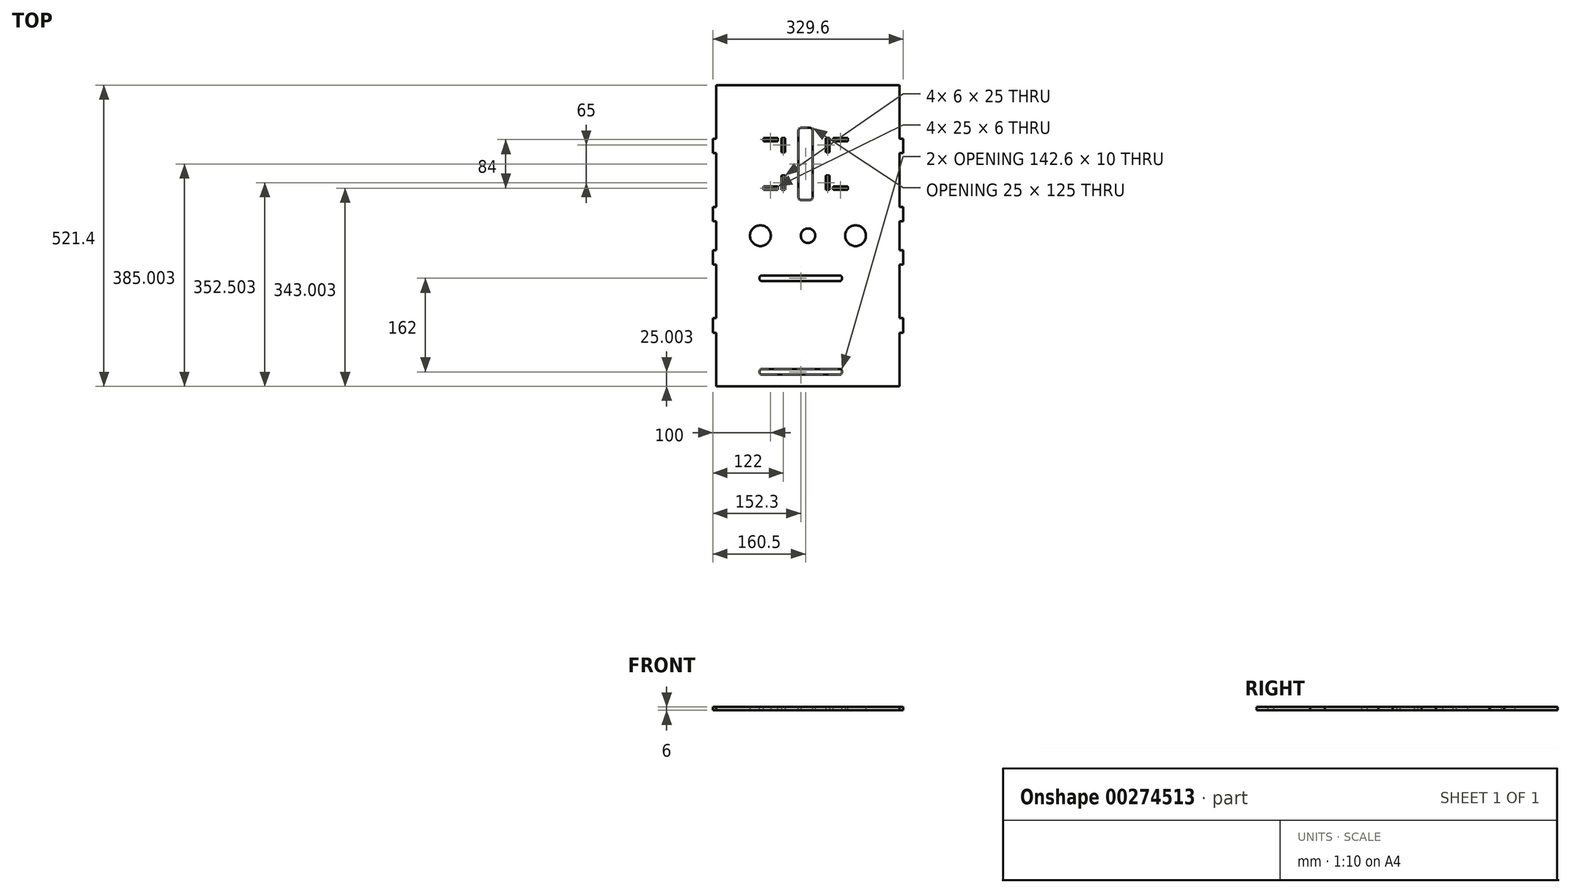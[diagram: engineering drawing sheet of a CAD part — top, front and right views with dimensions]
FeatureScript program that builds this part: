
annotation { "Feature Type Name" : "Feature", "Feature Type Description" : "" }
export const myFeature = defineFeature(function(context is Context, id is Id, definition is map)
    precondition{}
    {
        {
            var Q0;
            Q0=qCreatedBy(makeId("Top.planeOp"),FACE);
            var sketch = newSketch(context, id + "F0", { "sketchPlane" : qUnion([Q0])});
            skLineSegment(sketch, "E0.bottom", {"start": v(-164.8, 495.45) * mm, "end": v(164.8, 495.45) * mm});
            skLineSegment(sketch, "E0.top", {"start": v(-164.8, -25.95) * mm, "end": v(164.8, -25.95) * mm});
            skLineSegment(sketch, "E0.left", {"start": v(-164.8, 495.45) * mm, "end": v(-164.8, -25.95) * mm});
            skLineSegment(sketch, "E0.right", {"start": v(164.8, 495.45) * mm, "end": v(164.8, -25.95) * mm});
            skCircle(sketch, "E1", {"center": v(0, 234.75) * mm, "radius": 12.5 * mm});
            skCircle(sketch, "E2", {"center": v(-82.4, 234.75) * mm, "radius": 18 * mm});
            skCircle(sketch, "E3", {"center": v(82.4, 234.75) * mm, "radius": 18 * mm});
            skLineSegment(sketch, "E4.bottom", {"start": v(-45.8, 404.05) * mm, "end": v(-39.8, 404.05) * mm});
            skLineSegment(sketch, "E4.top", {"start": v(-45.8, 379.05) * mm, "end": v(-39.8, 379.05) * mm});
            skLineSegment(sketch, "E4.left", {"start": v(-45.8, 404.05) * mm, "end": v(-45.8, 379.05) * mm});
            skLineSegment(sketch, "E4.right", {"start": v(-39.8, 404.05) * mm, "end": v(-39.8, 379.05) * mm});
            skLineSegment(sketch, "E5.bottom", {"start": v(-45.8, 339.05) * mm, "end": v(-39.8, 339.05) * mm});
            skLineSegment(sketch, "E5.top", {"start": v(-45.8, 314.05) * mm, "end": v(-39.8, 314.05) * mm});
            skLineSegment(sketch, "E5.left", {"start": v(-45.8, 339.05) * mm, "end": v(-45.8, 314.05) * mm});
            skLineSegment(sketch, "E5.right", {"start": v(-39.8, 339.05) * mm, "end": v(-39.8, 314.05) * mm});
            skLineSegment(sketch, "E6.bottom", {"start": v(31.2, 404.05) * mm, "end": v(37.2, 404.05) * mm});
            skLineSegment(sketch, "E6.top", {"start": v(31.2, 379.05) * mm, "end": v(37.2, 379.05) * mm});
            skLineSegment(sketch, "E6.left", {"start": v(31.2, 404.05) * mm, "end": v(31.2, 379.05) * mm});
            skLineSegment(sketch, "E6.right", {"start": v(37.2, 404.05) * mm, "end": v(37.2, 379.05) * mm});
            skLineSegment(sketch, "E7.bottom", {"start": v(31.2, 339.05) * mm, "end": v(37.2, 339.05) * mm});
            skLineSegment(sketch, "E7.top", {"start": v(31.2, 314.05) * mm, "end": v(37.2, 314.05) * mm});
            skLineSegment(sketch, "E7.left", {"start": v(31.2, 339.05) * mm, "end": v(31.2, 314.05) * mm});
            skLineSegment(sketch, "E7.right", {"start": v(37.2, 339.05) * mm, "end": v(37.2, 314.05) * mm});
            skSolve(sketch);
        }
        {
            var Q0;
            Q0 = qSketchRegion(id + "F0", true);
            extrude(context, id + "F1", {"entities" : qUnion([Q0]), "depth" : 6 * mm});
        }
        {
            var Q0;
            Q0=makeQuery(id+"F1.opExtrude","CAP_FACE",FACE,{"disambiguationData":[OSD([sQuery(id+"F0.wireOp",EDGE,"E0.bottom"),sQuery(id+"F0.wireOp",EDGE,"E0.top"),sQuery(id+"F0.wireOp",EDGE,"E0.left"),sQuery(id+"F0.wireOp",EDGE,"E0.right"),sQuery(id+"F0.wireOp",EDGE,"E1")])],"isStart":false});
            var sketch = newSketch(context, id + "F2", { "sketchPlane" : qUnion([Q0])});
            skLineSegment(sketch, "E8.bottom", {"start": v(-164.8, 495.45) * mm, "end": v(-158.8, 495.45) * mm});
            skLineSegment(sketch, "E8.top", {"start": v(-164.8, 402.6) * mm, "end": v(-158.8, 402.6) * mm});
            skLineSegment(sketch, "E8.left", {"start": v(-164.8, 495.45) * mm, "end": v(-164.8, 402.6) * mm});
            skLineSegment(sketch, "E8.right", {"start": v(-158.8, 495.45) * mm, "end": v(-158.8, 402.6) * mm});
            skLineSegment(sketch, "E9.bottom", {"start": v(-164.8, 377.6) * mm, "end": v(-158.8, 377.6) * mm});
            skLineSegment(sketch, "E9.top", {"start": v(-164.8, 284.75) * mm, "end": v(-158.8, 284.75) * mm});
            skLineSegment(sketch, "E9.left", {"start": v(-164.8, 377.6) * mm, "end": v(-164.8, 284.75) * mm});
            skLineSegment(sketch, "E9.right", {"start": v(-158.8, 377.6) * mm, "end": v(-158.8, 284.75) * mm});
            skLineSegment(sketch, "E10.bottom", {"start": v(-164.8, 259.75) * mm, "end": v(-158.8, 259.75) * mm});
            skLineSegment(sketch, "E10.top", {"start": v(-164.8, 209.75) * mm, "end": v(-158.8, 209.75) * mm});
            skLineSegment(sketch, "E10.left", {"start": v(-164.8, 259.75) * mm, "end": v(-164.8, 209.75) * mm});
            skLineSegment(sketch, "E10.right", {"start": v(-158.8, 259.75) * mm, "end": v(-158.8, 209.75) * mm});
            skLineSegment(sketch, "E11.bottom", {"start": v(-164.8, 184.75) * mm, "end": v(-158.8, 184.75) * mm});
            skLineSegment(sketch, "E11.top", {"start": v(-164.8, 91.9) * mm, "end": v(-158.8, 91.9) * mm});
            skLineSegment(sketch, "E11.left", {"start": v(-164.8, 184.75) * mm, "end": v(-164.8, 91.9) * mm});
            skLineSegment(sketch, "E11.right", {"start": v(-158.8, 184.75) * mm, "end": v(-158.8, 91.9) * mm});
            skLineSegment(sketch, "E12.bottom", {"start": v(-164.8, -25.95) * mm, "end": v(-158.8, -25.95) * mm});
            skLineSegment(sketch, "E12.top", {"start": v(-164.8, 66.9) * mm, "end": v(-158.8, 66.9) * mm});
            skLineSegment(sketch, "E12.left", {"start": v(-164.8, -25.95) * mm, "end": v(-164.8, 66.9) * mm});
            skLineSegment(sketch, "E12.right", {"start": v(-158.8, -25.95) * mm, "end": v(-158.8, 66.9) * mm});
            skLineSegment(sketch, "E13", {"start": v(0, 495.45) * mm, "end": v(0, -25.95) * mm});
            skLineSegment(sketch, "E14.MirrorCS", {"start": v(164.8, 402.6) * mm, "end": v(158.8, 402.6) * mm});
            skLineSegment(sketch, "E15.MirrorCS", {"start": v(164.8, 66.9) * mm, "end": v(158.8, 66.9) * mm});
            skLineSegment(sketch, "E16.MirrorCS", {"start": v(164.8, 184.75) * mm, "end": v(158.8, 184.75) * mm});
            skLineSegment(sketch, "E17.MirrorCS", {"start": v(164.8, 377.6) * mm, "end": v(158.8, 377.6) * mm});
            skLineSegment(sketch, "E18.MirrorCS", {"start": v(164.8, 495.45) * mm, "end": v(158.8, 495.45) * mm});
            skLineSegment(sketch, "E19.MirrorCS", {"start": v(164.8, 284.75) * mm, "end": v(158.8, 284.75) * mm});
            skLineSegment(sketch, "E20.MirrorCS", {"start": v(164.8, -25.95) * mm, "end": v(158.8, -25.95) * mm});
            skLineSegment(sketch, "E21.MirrorCS", {"start": v(164.8, 209.75) * mm, "end": v(158.8, 209.75) * mm});
            skLineSegment(sketch, "E22.MirrorCS", {"start": v(164.8, 91.9) * mm, "end": v(158.8, 91.9) * mm});
            skLineSegment(sketch, "E23.MirrorCS", {"start": v(164.8, 259.75) * mm, "end": v(158.8, 259.75) * mm});
            skLineSegment(sketch, "E24.MirrorCS", {"start": v(158.8, -25.95) * mm, "end": v(158.8, 66.9) * mm});
            skLineSegment(sketch, "E25.MirrorCS", {"start": v(164.8, 495.45) * mm, "end": v(164.8, 402.6) * mm});
            skLineSegment(sketch, "E26.MirrorCS", {"start": v(158.8, 184.75) * mm, "end": v(158.8, 91.9) * mm});
            skLineSegment(sketch, "E27.MirrorCS", {"start": v(164.8, 377.6) * mm, "end": v(164.8, 284.75) * mm});
            skLineSegment(sketch, "E28.MirrorCS", {"start": v(158.8, 377.6) * mm, "end": v(158.8, 284.75) * mm});
            skLineSegment(sketch, "E29.MirrorCS", {"start": v(164.8, -25.95) * mm, "end": v(164.8, 66.9) * mm});
            skLineSegment(sketch, "E30.MirrorCS", {"start": v(158.8, 495.45) * mm, "end": v(158.8, 402.6) * mm});
            skLineSegment(sketch, "E31.MirrorCS", {"start": v(164.8, 259.75) * mm, "end": v(164.8, 209.75) * mm});
            skLineSegment(sketch, "E32.MirrorCS", {"start": v(158.8, 259.75) * mm, "end": v(158.8, 209.75) * mm});
            skLineSegment(sketch, "E33.MirrorCS", {"start": v(164.8, 184.75) * mm, "end": v(164.8, 91.9) * mm});
            skSolve(sketch);
        }
        {
            var Q0;
            Q0 = qSketchRegion(id + "F2", true);
            extrude(context, id + "F3", {"entities" : qUnion([Q0]), "operationType" : NewBodyOperationType.REMOVE, "oppositeDirection" : true, "depth" : 25 * mm});
        }
        {
            var Q0;
            Q0=makeQuery(id+"F1.opExtrude","CAP_FACE",FACE,{"disambiguationData":[OSD([sQuery(id+"F0.wireOp",EDGE,"E0.bottom"),sQuery(id+"F0.wireOp",EDGE,"E0.top"),sQuery(id+"F0.wireOp",EDGE,"E0.left"),sQuery(id+"F0.wireOp",EDGE,"E0.right"),sQuery(id+"F0.wireOp",EDGE,"E1")])],"isStart":false});
            var sketch = newSketch(context, id + "F4", { "sketchPlane" : qUnion([Q0])});
            skLineSegment(sketch, "E34.bottom", {"start": v(-79.8, 166.05) * mm, "end": v(54.8, 166.05) * mm});
            skLineSegment(sketch, "E34.top", {"start": v(-79.8, 156.05) * mm, "end": v(54.8, 156.05) * mm});
            skLineSegment(sketch, "E34.left", {"start": v(-83.8, 162.05) * mm, "end": v(-83.8, 160.05) * mm});
            skLineSegment(sketch, "E34.right", {"start": v(58.8, 162.05) * mm, "end": v(58.8, 160.05) * mm});
            skLineSegment(sketch, "E35.bottom", {"start": v(-79.8, 4.05) * mm, "end": v(54.8, 4.05) * mm});
            skLineSegment(sketch, "E35.top", {"start": v(-79.8, -5.95) * mm, "end": v(54.8, -5.95) * mm});
            skLineSegment(sketch, "E35.left", {"start": v(-83.8, 0.05) * mm, "end": v(-83.8, -1.95) * mm});
            skLineSegment(sketch, "E35.right", {"start": v(58.8, 0.05) * mm, "end": v(58.8, -1.95) * mm});
            skPoint(sketch, "E36.visualSharp", {"position": v(-83.8, 166.05) * mm});
            skArc(sketch, "E36.filletArc", {"start": v(-79.8, 166.05) * mm, "mid": v(-82.63, 164.88) * mm, "end": v(-83.8, 162.05) * mm});
            skPoint(sketch, "E37.visualSharp", {"position": v(58.8, 156.05) * mm});
            skArc(sketch, "E37.filletArc", {"start": v(54.8, 156.05) * mm, "mid": v(57.63, 157.22) * mm, "end": v(58.8, 160.05) * mm});
            skPoint(sketch, "E38.visualSharp", {"position": v(58.8, 166.05) * mm});
            skArc(sketch, "E38.filletArc", {"start": v(58.8, 162.05) * mm, "mid": v(57.63, 164.88) * mm, "end": v(54.8, 166.05) * mm});
            skPoint(sketch, "E39.visualSharp", {"position": v(-83.8, 4.05) * mm});
            skArc(sketch, "E39.filletArc", {"start": v(-79.8, 4.05) * mm, "mid": v(-82.63, 2.88) * mm, "end": v(-83.8, 0.05) * mm});
            skPoint(sketch, "E40.visualSharp", {"position": v(58.8, 4.05) * mm});
            skArc(sketch, "E40.filletArc", {"start": v(58.8, 0.05) * mm, "mid": v(57.63, 2.88) * mm, "end": v(54.8, 4.05) * mm});
            skPoint(sketch, "E41.visualSharp", {"position": v(58.8, -5.95) * mm});
            skArc(sketch, "E41.filletArc", {"start": v(54.8, -5.95) * mm, "mid": v(57.63, -4.78) * mm, "end": v(58.8, -1.95) * mm});
            skPoint(sketch, "E42.visualSharp", {"position": v(-83.8, -5.95) * mm});
            skArc(sketch, "E42.filletArc", {"start": v(-83.8, -1.95) * mm, "mid": v(-82.63, -4.78) * mm, "end": v(-79.8, -5.95) * mm});
            skPoint(sketch, "E43.visualSharp", {"position": v(-83.8, 156.05) * mm});
            skArc(sketch, "E43.filletArc", {"start": v(-83.8, 160.05) * mm, "mid": v(-82.63, 157.22) * mm, "end": v(-79.8, 156.05) * mm});
            skSolve(sketch);
        }
        {
            var Q0;
            Q0=makeQuery(id+"F1.opExtrude","CAP_FACE",FACE,{"disambiguationData":[OSD([sQuery(id+"F0.wireOp",EDGE,"E0.bottom"),sQuery(id+"F0.wireOp",EDGE,"E0.top"),sQuery(id+"F0.wireOp",EDGE,"E0.left"),sQuery(id+"F0.wireOp",EDGE,"E0.right"),sQuery(id+"F0.wireOp",EDGE,"E1"),sQuery(id+"F0.wireOp",EDGE,"E2"),sQuery(id+"F0.wireOp",EDGE,"E3"),sQuery(id+"F0.wireOp",EDGE,"E4.bottom"),sQuery(id+"F0.wireOp",EDGE,"E4.top"),sQuery(id+"F0.wireOp",EDGE,"E4.left"),sQuery(id+"F0.wireOp",EDGE,"E4.right"),sQuery(id+"F0.wireOp",EDGE,"E5.bottom"),sQuery(id+"F0.wireOp",EDGE,"E5.top"),sQuery(id+"F0.wireOp",EDGE,"E5.left"),sQuery(id+"F0.wireOp",EDGE,"E5.right"),sQuery(id+"F0.wireOp",EDGE,"E6.bottom"),sQuery(id+"F0.wireOp",EDGE,"E6.top"),sQuery(id+"F0.wireOp",EDGE,"E6.left"),sQuery(id+"F0.wireOp",EDGE,"E6.right"),sQuery(id+"F0.wireOp",EDGE,"E7.bottom"),sQuery(id+"F0.wireOp",EDGE,"E7.top"),sQuery(id+"F0.wireOp",EDGE,"E7.left"),sQuery(id+"F0.wireOp",EDGE,"E7.right")])],"isStart":false});
            var sketch = newSketch(context, id + "F5", { "sketchPlane" : qUnion([Q0])});
            skLineSegment(sketch, "E44.bottom", {"start": v(-77.3, 320.05) * mm, "end": v(-52.3, 320.05) * mm});
            skLineSegment(sketch, "E44.top", {"start": v(-77.3, 314.05) * mm, "end": v(-52.3, 314.05) * mm});
            skLineSegment(sketch, "E44.left", {"start": v(-77.3, 320.05) * mm, "end": v(-77.3, 314.05) * mm});
            skLineSegment(sketch, "E44.right", {"start": v(-52.3, 320.05) * mm, "end": v(-52.3, 314.05) * mm});
            skLineSegment(sketch, "E45.bottom", {"start": v(-52.3, 404.05) * mm, "end": v(-77.3, 404.05) * mm});
            skLineSegment(sketch, "E45.top", {"start": v(-52.3, 398.05) * mm, "end": v(-77.3, 398.05) * mm});
            skLineSegment(sketch, "E45.left", {"start": v(-52.3, 404.05) * mm, "end": v(-52.3, 398.05) * mm});
            skLineSegment(sketch, "E45.right", {"start": v(-77.3, 404.05) * mm, "end": v(-77.3, 398.05) * mm});
            skLineSegment(sketch, "E46.bottom", {"start": v(43.7, 404.05) * mm, "end": v(68.7, 404.05) * mm});
            skLineSegment(sketch, "E46.top", {"start": v(43.7, 398.05) * mm, "end": v(68.7, 398.05) * mm});
            skLineSegment(sketch, "E46.left", {"start": v(43.7, 404.05) * mm, "end": v(43.7, 398.05) * mm});
            skLineSegment(sketch, "E46.right", {"start": v(68.7, 404.05) * mm, "end": v(68.7, 398.05) * mm});
            skLineSegment(sketch, "E47.bottom", {"start": v(43.7, 314.05) * mm, "end": v(68.7, 314.05) * mm});
            skLineSegment(sketch, "E47.top", {"start": v(43.7, 320.05) * mm, "end": v(68.7, 320.05) * mm});
            skLineSegment(sketch, "E47.left", {"start": v(43.7, 314.05) * mm, "end": v(43.7, 320.05) * mm});
            skLineSegment(sketch, "E47.right", {"start": v(68.7, 314.05) * mm, "end": v(68.7, 320.05) * mm});
            skLineSegment(sketch, "E48.bottom", {"start": v(-11.8, 421.55) * mm, "end": v(3.2, 421.55) * mm});
            skLineSegment(sketch, "E48.top", {"start": v(-11.8, 296.55) * mm, "end": v(3.2, 296.55) * mm});
            skLineSegment(sketch, "E48.left", {"start": v(-16.8, 416.55) * mm, "end": v(-16.8, 301.55) * mm});
            skLineSegment(sketch, "E48.right", {"start": v(8.2, 416.55) * mm, "end": v(8.2, 301.55) * mm});
            skPoint(sketch, "E49.visualSharp", {"position": v(-16.8, 421.55) * mm});
            skArc(sketch, "E49.filletArc", {"start": v(-11.8, 421.55) * mm, "mid": v(-15.34, 420.09) * mm, "end": v(-16.8, 416.55) * mm});
            skPoint(sketch, "E50.visualSharp", {"position": v(8.2, 421.55) * mm});
            skArc(sketch, "E50.filletArc", {"start": v(8.2, 416.55) * mm, "mid": v(6.74, 420.09) * mm, "end": v(3.2, 421.55) * mm});
            skPoint(sketch, "E51.visualSharp", {"position": v(8.2, 296.55) * mm});
            skArc(sketch, "E51.filletArc", {"start": v(3.2, 296.55) * mm, "mid": v(6.74, 298.02) * mm, "end": v(8.2, 301.55) * mm});
            skPoint(sketch, "E52.visualSharp", {"position": v(-16.8, 296.55) * mm});
            skArc(sketch, "E52.filletArc", {"start": v(-16.8, 301.55) * mm, "mid": v(-15.34, 298.02) * mm, "end": v(-11.8, 296.55) * mm});
            skSolve(sketch);
        }
        {
            var Q0;
            Q0 = qSketchRegion(id + "F5", true);
            extrude(context, id + "F6", {"entities" : qUnion([Q0]), "operationType" : NewBodyOperationType.REMOVE, "oppositeDirection" : true, "depth" : 25 * mm});
        }
        {
            var Q0;
            Q0 = qSketchRegion(id + "F4", true);
            extrude(context, id + "F7", {"entities" : qUnion([Q0]), "operationType" : NewBodyOperationType.REMOVE, "oppositeDirection" : true, "depth" : 25 * mm});
        }
    });
